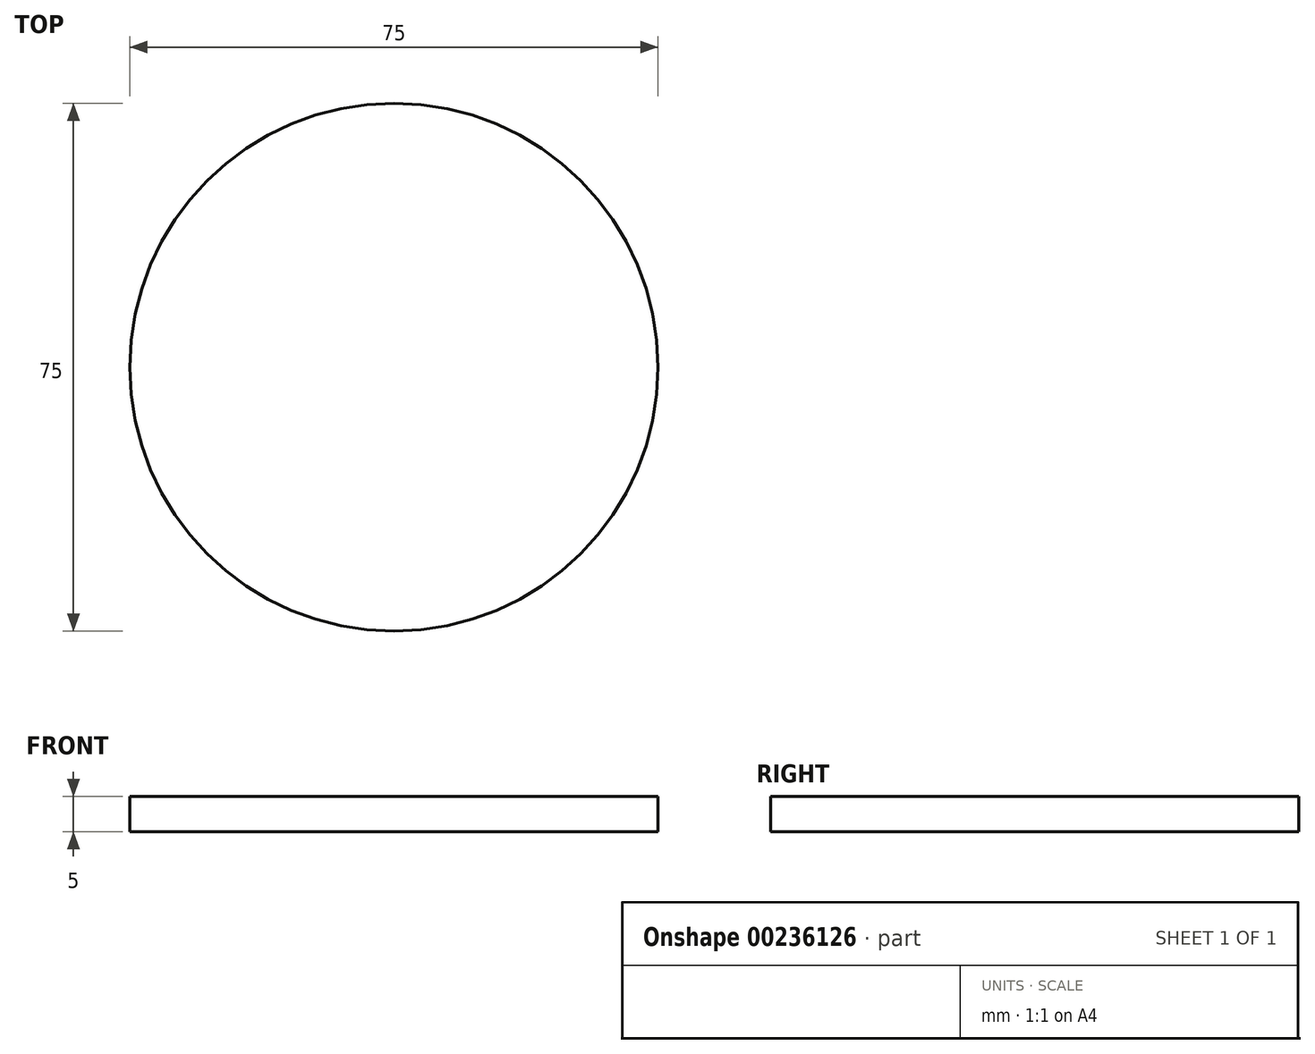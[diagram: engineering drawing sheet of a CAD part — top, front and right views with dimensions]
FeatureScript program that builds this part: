
annotation { "Feature Type Name" : "Feature", "Feature Type Description" : "" }
export const myFeature = defineFeature(function(context is Context, id is Id, definition is map)
    precondition{}
    {
        {
            var Q0;
            Q0=qCreatedBy(makeId("Top.planeOp"),FACE);
            var sketch = newSketch(context, id + "F0", { "sketchPlane" : qUnion([Q0])});
            skCircle(sketch, "E0", {"center": v(0, 0) * mm, "radius": 37.5 * mm});
            skSolve(sketch);
        }
        {
            var Q0;
            Q0=makeQuery(id+"F0.imprint","IMPRINT",FACE,{"disambiguationData":[TD([[makeQuery(id+"F0.imprint","IMPRINT",EDGE,{"derivedFrom":sQuery(id+"F0.wireOp",EDGE,"E0")}),1.0]])]});
            extrude(context, id + "F1", {"entities" : qUnion([Q0]), "endBound" : BoundingType.SYMMETRIC, "oppositeDirection" : true, "depth" : 5 * mm});
        }
    });
